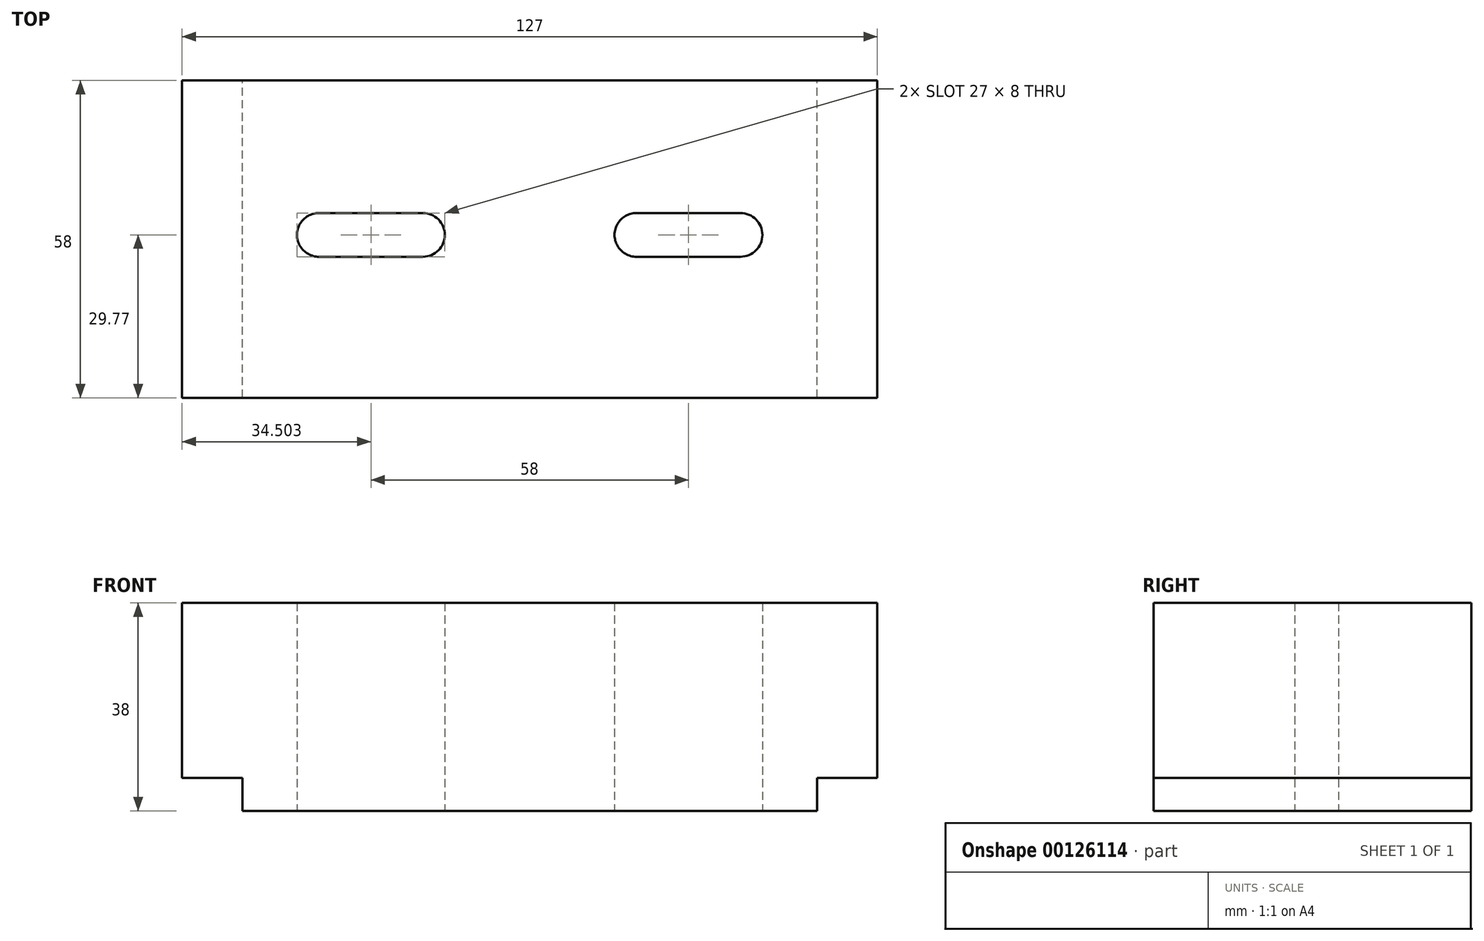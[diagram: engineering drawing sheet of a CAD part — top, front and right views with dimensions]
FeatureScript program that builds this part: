
annotation { "Feature Type Name" : "Feature", "Feature Type Description" : "" }
export const myFeature = defineFeature(function(context is Context, id is Id, definition is map)
    precondition{}
    {
        {
            var Q0;
            Q0=qCreatedBy(makeId("Top.planeOp"),FACE);
            var sketch = newSketch(context, id + "F0", { "sketchPlane" : qUnion([Q0])});
            skLineSegment(sketch, "E0.bottom", {"start": v(-91.16, 28.23) * mm, "end": v(35.84, 28.23) * mm});
            skLineSegment(sketch, "E0.top", {"start": v(-91.16, -29.77) * mm, "end": v(35.84, -29.77) * mm});
            skLineSegment(sketch, "E0.left", {"start": v(-91.16, 28.23) * mm, "end": v(-91.16, -29.77) * mm});
            skLineSegment(sketch, "E0.right", {"start": v(35.84, 28.23) * mm, "end": v(35.84, -29.77) * mm});
            skSolve(sketch);
        }
        {
            var Q0;
            Q0 = qSketchRegion(id + "F0", true);
            extrude(context, id + "F1", {"entities" : qUnion([Q0]), "depth" : 38 * mm});
        }
        {
            var Q0;
            Q0=qCreatedBy(makeId("Top.planeOp"),FACE);
            var sketch = newSketch(context, id + "F2", { "sketchPlane" : qUnion([Q0])});
            skCircle(sketch, "E1", {"center": v(-47.16, 0) * mm, "radius": 4 * mm});
            skCircle(sketch, "E2", {"center": v(-8.16, 0) * mm, "radius": 4 * mm});
            skCircle(sketch, "E3", {"center": v(-66.16, 0) * mm, "radius": 4 * mm});
            skCircle(sketch, "E4", {"center": v(10.84, 0) * mm, "radius": 4 * mm});
            skLineSegment(sketch, "E5", {"start": v(-66.14, 4) * mm, "end": v(-47.16, 4) * mm});
            skLineSegment(sketch, "E6", {"start": v(-66.14, -4) * mm, "end": v(-47.16, -4) * mm});
            skLineSegment(sketch, "E7", {"start": v(-8.13, 4) * mm, "end": v(10.84, 4) * mm});
            skLineSegment(sketch, "E8", {"start": v(-8.16, -4) * mm, "end": v(10.84, -4) * mm});
            skSolve(sketch);
        }
        {
            var Q0;
            {var subQ0=sQuery(id+"F2.wireOp",EDGE,"E3");var subQ1=makeQuery(id+"F2.imprint","INTERSECT",VERTEX,{"derivedFrom":[subQ0,sQuery(id+"F2.wireOp",EDGE,"E5")]});Q0=makeQuery(id+"F2.imprint","IMPRINT",FACE,{"disambiguationData":[TD([[makeQuery(id+"F2.imprint","IMPRINT",EDGE,{"disambiguationData":[TD([[subQ1,-1.0]])],"derivedFrom":subQ0}),1.0]])]});}
            var Q1;
            {var subQ0=sQuery(id+"F2.wireOp",EDGE,"E1");var subQ1=makeQuery(id+"F2.imprint","INTERSECT",VERTEX,{"derivedFrom":[subQ0,sQuery(id+"F2.wireOp",EDGE,"E5")]});Q1=makeQuery(id+"F2.imprint","IMPRINT",FACE,{"disambiguationData":[TD([[makeQuery(id+"F2.imprint","IMPRINT",EDGE,{"disambiguationData":[TD([[subQ1,-1.0]])],"derivedFrom":subQ0}),1.0]])]});}
            var Q2;
            {var subQ0=sQuery(id+"F2.wireOp",EDGE,"E5");Q2=makeQuery(id+"F2.imprint","IMPRINT",FACE,{"disambiguationData":[TD([[makeQuery(id+"F2.imprint","IMPRINT",EDGE,{"derivedFrom":subQ0}),-1.0]])]});}
            var Q3;
            {var subQ0=sQuery(id+"F2.wireOp",EDGE,"E2");var subQ1=makeQuery(id+"F2.imprint","INTERSECT",VERTEX,{"derivedFrom":[subQ0,sQuery(id+"F2.wireOp",EDGE,"E7")]});Q3=makeQuery(id+"F2.imprint","IMPRINT",FACE,{"disambiguationData":[TD([[makeQuery(id+"F2.imprint","IMPRINT",EDGE,{"disambiguationData":[TD([[subQ1,-1.0]])],"derivedFrom":subQ0}),1.0]])]});}
            var Q4;
            {var subQ0=sQuery(id+"F2.wireOp",EDGE,"E7");Q4=makeQuery(id+"F2.imprint","IMPRINT",FACE,{"disambiguationData":[TD([[makeQuery(id+"F2.imprint","IMPRINT",EDGE,{"derivedFrom":subQ0}),-1.0]])]});}
            var Q5;
            {var subQ0=sQuery(id+"F2.wireOp",EDGE,"E4");var subQ1=makeQuery(id+"F2.imprint","INTERSECT",VERTEX,{"derivedFrom":[subQ0,sQuery(id+"F2.wireOp",EDGE,"E7")]});Q5=makeQuery(id+"F2.imprint","IMPRINT",FACE,{"disambiguationData":[TD([[makeQuery(id+"F2.imprint","IMPRINT",EDGE,{"disambiguationData":[TD([[subQ1,-1.0]])],"derivedFrom":subQ0}),1.0]])]});}
            extrude(context, id + "F3", {"entities" : qUnion([Q0, Q1, Q2, Q3, Q4, Q5]), "operationType" : NewBodyOperationType.REMOVE, "endBound" : BoundingType.THROUGH_ALL, "depth" : 25.4 * mm});
        }
        {
            var Q0;
            Q0=qCreatedBy(makeId("Front.planeOp"),FACE);
            var sketch = newSketch(context, id + "F4", { "sketchPlane" : qUnion([Q0])});
            skLineSegment(sketch, "E9.bottom", {"start": v(35.84, 0) * mm, "end": v(24.84, 0) * mm});
            skLineSegment(sketch, "E9.top", {"start": v(35.84, 6) * mm, "end": v(24.84, 6) * mm});
            skLineSegment(sketch, "E9.left", {"start": v(35.84, 0) * mm, "end": v(35.84, 6) * mm});
            skLineSegment(sketch, "E9.right", {"start": v(24.84, 0) * mm, "end": v(24.84, 6) * mm});
            skSolve(sketch);
        }
        {
            var Q0;
            Q0 = qSketchRegion(id + "F4", true);
            extrude(context, id + "F5", {"entities" : qUnion([Q0]), "operationType" : NewBodyOperationType.REMOVE, "endBound" : BoundingType.SYMMETRIC, "depth" : 101.6 * mm});
        }
        {
            var Q0;
            Q0=qCreatedBy(makeId("Front.planeOp"),FACE);
            var sketch = newSketch(context, id + "F6", { "sketchPlane" : qUnion([Q0])});
            skLineSegment(sketch, "E10.bottom", {"start": v(-91.16, 6) * mm, "end": v(-80.16, 6) * mm});
            skLineSegment(sketch, "E10.top", {"start": v(-91.16, 0) * mm, "end": v(-80.16, 0) * mm});
            skLineSegment(sketch, "E10.left", {"start": v(-91.16, 6) * mm, "end": v(-91.16, 0) * mm});
            skLineSegment(sketch, "E10.right", {"start": v(-80.16, 6) * mm, "end": v(-80.16, 0) * mm});
            skSolve(sketch);
        }
        {
            var Q0;
            Q0 = qSketchRegion(id + "F6", true);
            extrude(context, id + "F7", {"entities" : qUnion([Q0]), "operationType" : NewBodyOperationType.REMOVE, "endBound" : BoundingType.SYMMETRIC, "depth" : 101.6 * mm});
        }
    });
